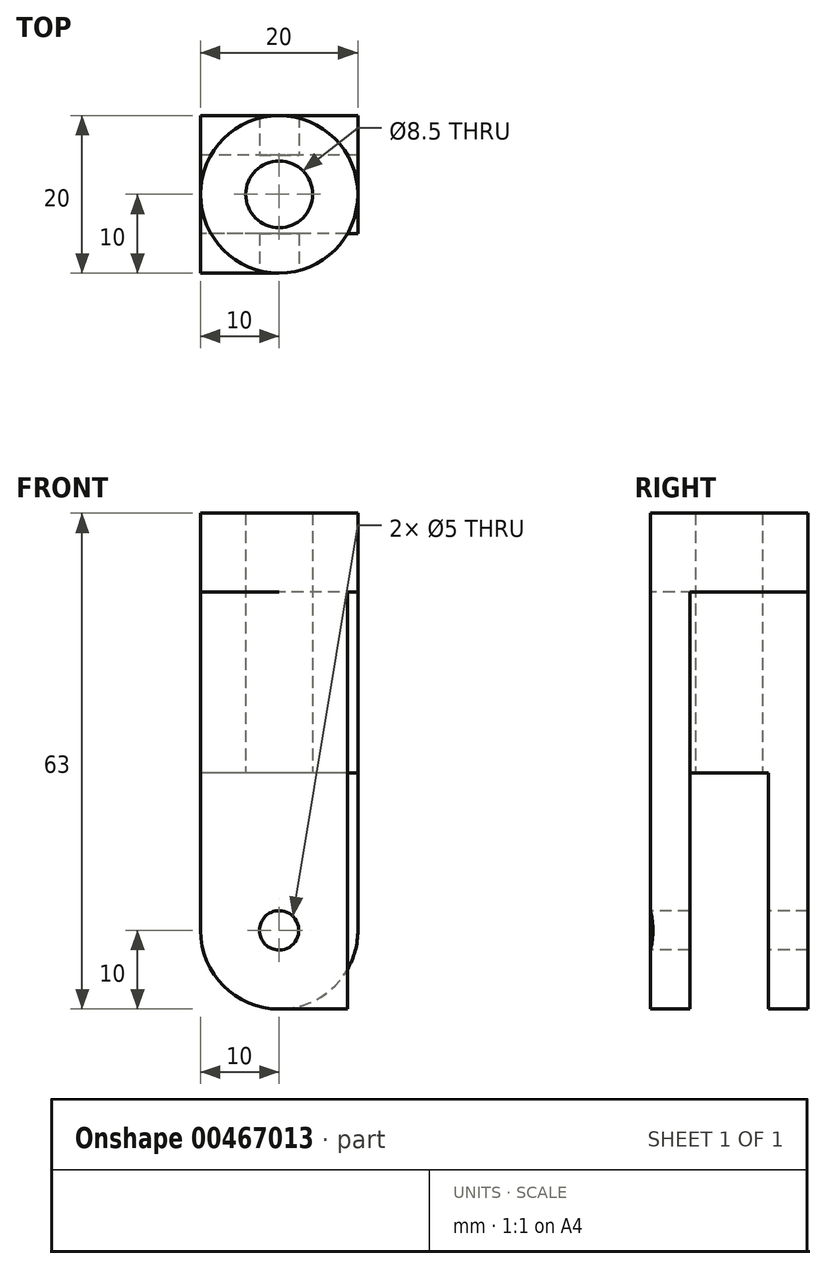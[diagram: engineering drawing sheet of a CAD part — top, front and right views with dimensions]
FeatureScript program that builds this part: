
annotation { "Feature Type Name" : "Feature", "Feature Type Description" : "" }
export const myFeature = defineFeature(function(context is Context, id is Id, definition is map)
    precondition{}
    {
        {
            var Q0;
            Q0=qCreatedBy(makeId("Top.planeOp"),FACE);
            var sketch = newSketch(context, id + "F0", { "sketchPlane" : qUnion([Q0])});
            skCircle(sketch, "E0", {"center": v(0, 0) * mm, "radius": 10 * mm});
            skCircle(sketch, "E1", {"center": v(0, 0) * mm, "radius": 4.25 * mm});
            skSolve(sketch);
        }
        {
            var Q0;
            Q0 = qSketchRegion(id + "F0", true);
            extrude(context, id + "F1", {"entities" : qUnion([Q0]), "depth" : 10 * mm});
        }
        {
            var Q0;
            Q0=makeQuery(id+"F0.imprint","IMPRINT",FACE,{"disambiguationData":[TD([[makeQuery(id+"F0.imprint","IMPRINT",EDGE,{"derivedFrom":sQuery(id+"F0.wireOp",EDGE,"E0")}),1.0]])]});
            var sketch = newSketch(context, id + "F2", { "sketchPlane" : qUnion([Q0])});
            skLineSegment(sketch, "E2.top", {"start": v(0, -10) * mm, "end": v(10, -10) * mm});
            skLineSegment(sketch, "E2.right", {"start": v(10, -5) * mm, "end": v(10, -10) * mm});
            skLineSegment(sketch, "E3.bottom", {"start": v(10, -10) * mm, "end": v(-10, -10) * mm});
            skLineSegment(sketch, "E3.left", {"start": v(10, -10) * mm, "end": v(10, -5) * mm});
            skLineSegment(sketch, "E4.top", {"start": v(10, -5) * mm, "end": v(-10, -5) * mm});
            skLineSegment(sketch, "E4.right", {"start": v(-10, -10) * mm, "end": v(-10, -5) * mm});
            skLineSegment(sketch, "E5", {"start": v(10, 0) * mm, "end": v(-10, 0) * mm});
            skLineSegment(sketch, "E6.MirrorCS", {"start": v(10, 5) * mm, "end": v(-10, 5) * mm});
            skLineSegment(sketch, "E7.MirrorCS", {"start": v(10, 10) * mm, "end": v(10, 5) * mm});
            skLineSegment(sketch, "E8.MirrorCS", {"start": v(10, 10) * mm, "end": v(-10, 10) * mm});
            skLineSegment(sketch, "E9.MirrorCS", {"start": v(-10, 10) * mm, "end": v(-10, 5) * mm});
            skLineSegment(sketch, "E10", {"start": v(10, -5) * mm, "end": v(10, 5) * mm});
            skLineSegment(sketch, "E11", {"start": v(-10, 5) * mm, "end": v(-10, -5) * mm});
            skSolve(sketch);
        }
        {
            var Q0;
            {var subQ0=sQuery(id+"F2.wireOp",EDGE,"E3.left");Q0=makeQuery(id+"F2.imprint","IMPRINT",FACE,{"disambiguationData":[TD([[makeQuery(id+"F2.imprint","IMPRINT",EDGE,{"derivedFrom":subQ0}),1.0]])]});}
            var Q1;
            {var subQ0=makeQuery(id+"F0.imprint","IMPRINT",EDGE,{"derivedFrom":sQuery(id+"F0.wireOp",EDGE,"E0")});var subQ2=sQuery(id+"F2.wireOp",EDGE,"E4.top");var subQ3=makeQuery(id+"F2.imprint","INTERSECT",VERTEX,{"disambiguationData":[OD(0.0)],"derivedFrom":[subQ0,subQ2]});Q1=makeQuery(id+"F2.imprint","IMPRINT",FACE,{"disambiguationData":[TD([[makeQuery(id+"F2.imprint","IMPRINT",EDGE,{"disambiguationData":[TD([[subQ3,-1.0]])],"derivedFrom":subQ2}),1.0]])]});}
            var Q2;
            {var subQ0=sQuery(id+"F2.wireOp",EDGE,"E4.right");Q2=makeQuery(id+"F2.imprint","IMPRINT",FACE,{"disambiguationData":[TD([[makeQuery(id+"F2.imprint","IMPRINT",EDGE,{"derivedFrom":subQ0}),-1.0]])]});}
            var Q3;
            {var subQ0=sQuery(id+"F2.wireOp",EDGE,"E7.MirrorCS");Q3=makeQuery(id+"F2.imprint","IMPRINT",FACE,{"disambiguationData":[TD([[makeQuery(id+"F2.imprint","IMPRINT",EDGE,{"derivedFrom":subQ0}),-1.0]])]});}
            var Q4;
            {var subQ0=sQuery(id+"F2.wireOp",EDGE,"E9.MirrorCS");Q4=makeQuery(id+"F2.imprint","IMPRINT",FACE,{"disambiguationData":[TD([[makeQuery(id+"F2.imprint","IMPRINT",EDGE,{"derivedFrom":subQ0}),1.0]])]});}
            var Q5;
            {var subQ0=makeQuery(id+"F0.imprint","IMPRINT",EDGE,{"derivedFrom":sQuery(id+"F0.wireOp",EDGE,"E0")});var subQ2=sQuery(id+"F2.wireOp",EDGE,"E6.MirrorCS");var subQ4=makeQuery(id+"F2.imprint","INTERSECT",VERTEX,{"disambiguationData":[OD(0.0)],"derivedFrom":[subQ0,subQ2]});Q5=makeQuery(id+"F2.imprint","IMPRINT",FACE,{"disambiguationData":[TD([[makeQuery(id+"F2.imprint","IMPRINT",EDGE,{"disambiguationData":[TD([[subQ4,-1.0]])],"derivedFrom":subQ2}),-1.0]])]});}
            var Q6;
            {var subQ0=sQuery(id+"F2.wireOp",EDGE,"E6.MirrorCS");var subQ1=makeQuery(id+"F0.imprint","IMPRINT",EDGE,{"derivedFrom":sQuery(id+"F0.wireOp",EDGE,"E1")});var subQ2=makeQuery(id+"F2.imprint","INTERSECT",VERTEX,{"disambiguationData":[OD(0.0)],"derivedFrom":[subQ1,subQ0]});Q6=makeQuery(id+"F2.imprint","IMPRINT",FACE,{"disambiguationData":[TD([[makeQuery(id+"F2.imprint","IMPRINT",EDGE,{"disambiguationData":[TD([[subQ2,-1.0]])],"derivedFrom":subQ0}),-1.0]])]});}
            var Q7;
            {var subQ0=sQuery(id+"F2.wireOp",EDGE,"E4.top");var subQ1=makeQuery(id+"F0.imprint","IMPRINT",EDGE,{"derivedFrom":sQuery(id+"F0.wireOp",EDGE,"E1")});var subQ2=makeQuery(id+"F2.imprint","INTERSECT",VERTEX,{"disambiguationData":[OD(0.0)],"derivedFrom":[subQ1,subQ0]});Q7=makeQuery(id+"F2.imprint","IMPRINT",FACE,{"disambiguationData":[TD([[makeQuery(id+"F2.imprint","IMPRINT",EDGE,{"disambiguationData":[TD([[subQ2,-1.0]])],"derivedFrom":subQ0}),1.0]])]});}
            extrude(context, id + "F3", {"entities" : qUnion([Q0, Q1, Q2, Q3, Q4, Q5, Q6, Q7]), "operationType" : NewBodyOperationType.ADD, "oppositeDirection" : true, "depth" : 53 * mm, "offsetDistance" : 25 * mm});
        }
        {
            var Q0;
            Q0=makeQuery(id+"F3.opExtrude","SWEPT_FACE",FACE,{"disambiguationData":[OSD([sQuery(id+"F2.wireOp",EDGE,"E3.bottom")])]});
            var sketch = newSketch(context, id + "F4", { "sketchPlane" : qUnion([Q0])});
            skLineSegment(sketch, "E12", {"start": v(0, -53) * mm, "end": v(0, -43) * mm});
            skPoint(sketch, "E12.endSnap0", {"position": v(0, -53) * mm});
            skCircle(sketch, "E13", {"center": v(0, -43) * mm, "radius": 2.5 * mm});
            skSolve(sketch);
        }
        {
            var Q0;
            Q0=makeQuery(id+"F4.imprint","IMPRINT",FACE,{"disambiguationData":[TD([[makeQuery(id+"F4.imprint","IMPRINT",EDGE,{"derivedFrom":sQuery(id+"F4.wireOp",EDGE,"E13")}),1.0]])]});
            extrude(context, id + "F5", {"entities" : qUnion([Q0]), "operationType" : NewBodyOperationType.REMOVE, "oppositeDirection" : true, "depth" : 25 * mm});
        }
        {
            var Q0;
            {var subQ0=sQuery(id+"F2.wireOp",EDGE,"E5");var subQ1=makeQuery(id+"F0.imprint","IMPRINT",EDGE,{"derivedFrom":sQuery(id+"F0.wireOp",EDGE,"E1")});var subQ2=makeQuery(id+"F2.imprint","INTERSECT",VERTEX,{"disambiguationData":[OD(0.0)],"derivedFrom":[subQ1,subQ0]});Q0=makeQuery(id+"F2.imprint","IMPRINT",FACE,{"disambiguationData":[TD([[makeQuery(id+"F2.imprint","IMPRINT",EDGE,{"disambiguationData":[TD([[subQ2,-1.0]])],"derivedFrom":subQ0}),-1.0]])]});}
            var Q1;
            {var subQ0=sQuery(id+"F2.wireOp",EDGE,"E4.top");var subQ1=makeQuery(id+"F0.imprint","IMPRINT",EDGE,{"derivedFrom":sQuery(id+"F0.wireOp",EDGE,"E1")});var subQ2=makeQuery(id+"F2.imprint","INTERSECT",VERTEX,{"disambiguationData":[OD(0.0)],"derivedFrom":[subQ1,subQ0]});Q1=makeQuery(id+"F2.imprint","IMPRINT",FACE,{"disambiguationData":[TD([[makeQuery(id+"F2.imprint","IMPRINT",EDGE,{"disambiguationData":[TD([[subQ2,-1.0]])],"derivedFrom":subQ0}),-1.0]])]});}
            var Q2;
            {var subQ0=sQuery(id+"F2.wireOp",EDGE,"E4.top");var subQ1=makeQuery(id+"F0.imprint","IMPRINT",EDGE,{"derivedFrom":sQuery(id+"F0.wireOp",EDGE,"E0")});var subQ2=makeQuery(id+"F2.imprint","INTERSECT",VERTEX,{"disambiguationData":[OD(0.0)],"derivedFrom":[subQ1,subQ0]});Q2=makeQuery(id+"F2.imprint","IMPRINT",FACE,{"disambiguationData":[TD([[makeQuery(id+"F2.imprint","IMPRINT",EDGE,{"disambiguationData":[TD([[subQ2,-1.0]])],"derivedFrom":subQ0}),-1.0]])]});}
            var Q3;
            {var subQ1=makeQuery(id+"F0.imprint","IMPRINT",EDGE,{"derivedFrom":sQuery(id+"F0.wireOp",EDGE,"E0")});var subQ5=sQuery(id+"F2.wireOp",EDGE,"E6.MirrorCS");var subQ6=makeQuery(id+"F2.imprint","INTERSECT",VERTEX,{"disambiguationData":[OD(0.0)],"derivedFrom":[subQ1,subQ5]});Q3=makeQuery(id+"F2.imprint","IMPRINT",FACE,{"disambiguationData":[TD([[makeQuery(id+"F2.imprint","IMPRINT",EDGE,{"disambiguationData":[TD([[subQ6,-1.0]])],"derivedFrom":subQ5}),1.0]])]});}
            var Q4;
            {var subQ3=makeQuery(id+"F0.imprint","IMPRINT",EDGE,{"derivedFrom":sQuery(id+"F0.wireOp",EDGE,"E1")});var subQ5=sQuery(id+"F2.wireOp",EDGE,"E6.MirrorCS");var subQ6=makeQuery(id+"F2.imprint","INTERSECT",VERTEX,{"disambiguationData":[OD(1.0)],"derivedFrom":[subQ3,subQ5]});Q4=makeQuery(id+"F2.imprint","IMPRINT",FACE,{"disambiguationData":[TD([[makeQuery(id+"F2.imprint","IMPRINT",EDGE,{"disambiguationData":[TD([[subQ6,-1.0]])],"derivedFrom":subQ5}),1.0]])]});}
            var Q5;
            {var subQ0=sQuery(id+"F2.wireOp",EDGE,"E4.top");var subQ1=makeQuery(id+"F0.imprint","IMPRINT",EDGE,{"derivedFrom":sQuery(id+"F0.wireOp",EDGE,"E1")});var subQ2=makeQuery(id+"F2.imprint","INTERSECT",VERTEX,{"disambiguationData":[OD(1.0)],"derivedFrom":[subQ1,subQ0]});Q5=makeQuery(id+"F2.imprint","IMPRINT",FACE,{"disambiguationData":[TD([[makeQuery(id+"F2.imprint","IMPRINT",EDGE,{"disambiguationData":[TD([[subQ2,-1.0]])],"derivedFrom":subQ0}),-1.0]])]});}
            var Q6;
            {var subQ1=sQuery(id+"F2.wireOp",EDGE,"E6.MirrorCS");var subQ3=makeQuery(id+"F0.imprint","IMPRINT",EDGE,{"derivedFrom":sQuery(id+"F0.wireOp",EDGE,"E0")});var subQ4=makeQuery(id+"F2.imprint","INTERSECT",VERTEX,{"disambiguationData":[OD(1.0)],"derivedFrom":[subQ3,subQ1]});Q6=makeQuery(id+"F2.imprint","IMPRINT",FACE,{"disambiguationData":[TD([[makeQuery(id+"F2.imprint","IMPRINT",EDGE,{"disambiguationData":[TD([[subQ4,-1.0]])],"derivedFrom":subQ1}),1.0]])]});}
            var Q7;
            {var subQ1=sQuery(id+"F2.wireOp",EDGE,"E4.top");var subQ3=makeQuery(id+"F0.imprint","IMPRINT",EDGE,{"derivedFrom":sQuery(id+"F0.wireOp",EDGE,"E0")});var subQ4=makeQuery(id+"F2.imprint","INTERSECT",VERTEX,{"disambiguationData":[OD(1.0)],"derivedFrom":[subQ3,subQ1]});Q7=makeQuery(id+"F2.imprint","IMPRINT",FACE,{"disambiguationData":[TD([[makeQuery(id+"F2.imprint","IMPRINT",EDGE,{"disambiguationData":[TD([[subQ4,-1.0]])],"derivedFrom":subQ1}),-1.0]])]});}
            var Q8;
            {var subQ1=sQuery(id+"F2.wireOp",EDGE,"E6.MirrorCS");var subQ3=makeQuery(id+"F0.imprint","IMPRINT",EDGE,{"derivedFrom":sQuery(id+"F0.wireOp",EDGE,"E0")});var subQ4=makeQuery(id+"F2.imprint","INTERSECT",VERTEX,{"disambiguationData":[OD(0.0)],"derivedFrom":[subQ3,subQ1]});Q8=makeQuery(id+"F2.imprint","IMPRINT",FACE,{"disambiguationData":[TD([[makeQuery(id+"F2.imprint","IMPRINT",EDGE,{"disambiguationData":[TD([[subQ4,1.0]])],"derivedFrom":subQ1}),1.0]])]});}
            var Q9;
            {var subQ1=sQuery(id+"F2.wireOp",EDGE,"E4.top");var subQ3=makeQuery(id+"F0.imprint","IMPRINT",EDGE,{"derivedFrom":sQuery(id+"F0.wireOp",EDGE,"E0")});var subQ4=makeQuery(id+"F2.imprint","INTERSECT",VERTEX,{"disambiguationData":[OD(0.0)],"derivedFrom":[subQ3,subQ1]});Q9=makeQuery(id+"F2.imprint","IMPRINT",FACE,{"disambiguationData":[TD([[makeQuery(id+"F2.imprint","IMPRINT",EDGE,{"disambiguationData":[TD([[subQ4,1.0]])],"derivedFrom":subQ1}),-1.0]])]});}
            var Q10;
            {var subQ0=sQuery(id+"F2.wireOp",EDGE,"E5");var subQ1=makeQuery(id+"F0.imprint","IMPRINT",EDGE,{"derivedFrom":sQuery(id+"F0.wireOp",EDGE,"E1")});var subQ2=makeQuery(id+"F2.imprint","INTERSECT",VERTEX,{"disambiguationData":[OD(0.0)],"derivedFrom":[subQ1,subQ0]});Q10=makeQuery(id+"F2.imprint","IMPRINT",FACE,{"disambiguationData":[TD([[makeQuery(id+"F2.imprint","IMPRINT",EDGE,{"disambiguationData":[TD([[subQ2,-1.0]])],"derivedFrom":subQ0}),1.0]])]});}
            extrude(context, id + "F6", {"entities" : qUnion([Q0, Q1, Q2, Q3, Q4, Q5, Q6, Q7, Q8, Q9, Q10]), "operationType" : NewBodyOperationType.ADD, "oppositeDirection" : true, "depth" : 23 * mm, "offsetDistance" : 25 * mm});
        }
        {
            var Q0;
            Q0=makeQuery(id+"F3.opExtrude","CAP_EDGE",EDGE,{"disambiguationData":[OSD([sQuery(id+"F2.wireOp",EDGE,"E4.right")])],"isStart":false});
            var Q1;
            Q1=makeQuery(id+"F3.opExtrude","CAP_EDGE",EDGE,{"disambiguationData":[OSD([sQuery(id+"F2.wireOp",EDGE,"E9.MirrorCS")])],"isStart":false});
            var Q2;
            Q2=makeQuery(id+"F3.opExtrude","CAP_EDGE",EDGE,{"disambiguationData":[OSD([sQuery(id+"F2.wireOp",EDGE,"E7.MirrorCS")])],"isStart":false});
            var Q3;
            Q3=makeQuery(id+"F3.opExtrude","CAP_EDGE",EDGE,{"disambiguationData":[OSD([sQuery(id+"F2.wireOp",EDGE,"E3.left")])],"isStart":false});
            fillet(context, id + "F7", {"entities" : qUnion([Q0, Q1, Q2, Q3]), "radius" : 10 * mm, "tangentPropagation" : true, "allowEdgeOverflow" : false});
        }
        {
            var Q0;
            Q0=sQuery(id+"F0.wireOp",VERTEX,"E0.center");
            var Q1;
            Q1=makeQuery(id+"F1.opExtrude","SWEPT_BODY",BODY,{"disambiguationData":[OSD([sQuery(id+"F0.wireOp",EDGE,"E0"),sQuery(id+"F0.wireOp",EDGE,"E1")])]});
            hole(context, id + "F8", {"style" : HoleStyle.SIMPLE, "endStyle" : HoleEndStyle.THROUGH, "holeDiameter" : 8.5 * mm, "isTappedThrough" : true, "tappedDepth" : 12 * mm, "tapClearance" : 3, "locations" : qUnion([Q0]), "scope" : qUnion([Q1])});
        }
    });
